# Revit family: СИБИТ_Узел_Перемычка_Высота 300 мм_D600 B2,5
name_source: partatom
category: Обобщенные модели
revit_build: Autodesk Revit 2017 (Build: 20171027_0315(x64)
units: mm (PartAtom-declared; Revit-internal decimal feet)

## family parameters
Всегда вертикально = Да
Заголовок OmniClass = Beams
Может служить основой для арматурных стержней = Нет
Номер OmniClass = 23.25.30.11.14.14
Общий = Да
Основа = Стена
При загрузке вырезать с полостями = Да
Размер круглого соединителя = Использовать диаметр
Тип детали = Нормальный
Точка расчета площади = Нет

## types (1)
- СИБИТ_Узел_Перемычка_Высота 300 мм_D600 B2,5
    Bimon = www.bimon.ru
    IFC Classification = Beam
    Omniclass Code = 23.25.30.11.14.14
    Omniclass Title = Beams
    SLT_1 = 1_LUT
    UNSPSC Code = 30101700
    UNSPSC Title = Beams
    URL = www.sibyt.ru
    Uniclass 2015 Code = EF_20_20
    Uniclass 2015 Title = Beams
    Д_тип_1 = Длина : 1200 мм
    Д_тип_2 = Длина : 1500 мм
    Д_тип_3 = Длина : 2000 мм
    Д_тип_4 = Длина : 2500 мм
    Изготовитель = СИБИТ
    Ключевая пометка = 04200.B2
    Контактный телефон = +7 (383) 363-90-90
    Материал несущих конструкций = СИБИТ_Перемычки_Газобетон D600 B2,5
    Разработчик модели = Bimon - сервисный провайдер услуг информационного моделирования
    Сертификат соответствия = https://sibyt.ru
    Тип_1 = Ширина : 100 мм
    Тип_2 = Ширина : 120 мм
    Тип_3 = Ширина : 150 мм
